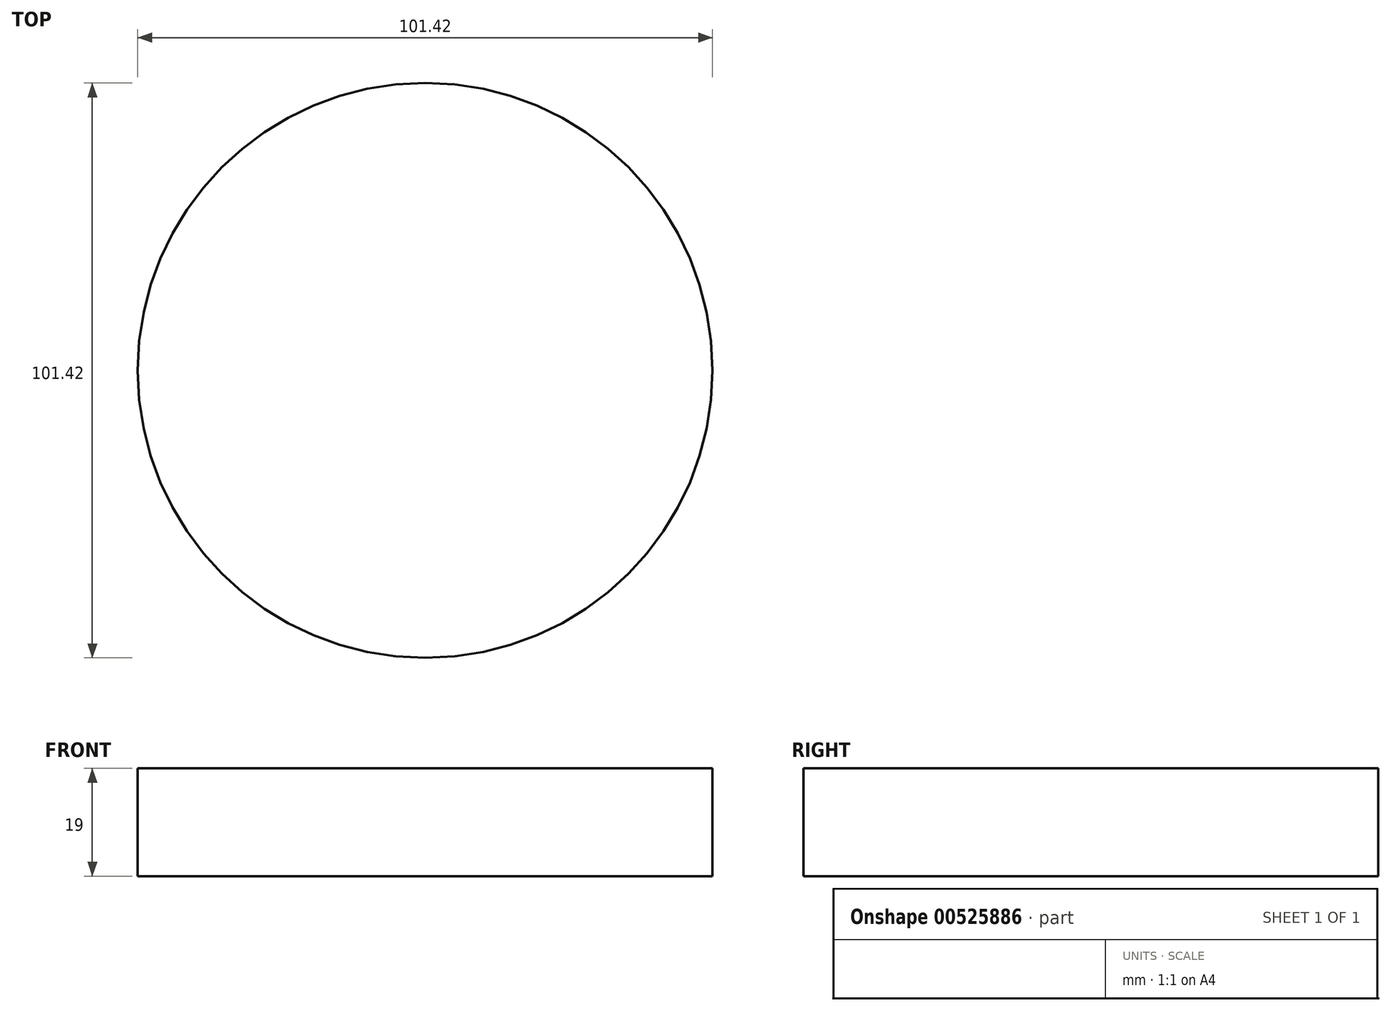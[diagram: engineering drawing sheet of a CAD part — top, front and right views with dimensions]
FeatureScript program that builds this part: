
annotation { "Feature Type Name" : "Feature", "Feature Type Description" : "" }
export const myFeature = defineFeature(function(context is Context, id is Id, definition is map)
    precondition{}
    {
        {
            var Q0;
            Q0=qCreatedBy(makeId("Top.planeOp"),FACE);
            var sketch = newSketch(context, id + "F0", { "sketchPlane" : qUnion([Q0])});
            skCircle(sketch, "E0", {"center": v(0, 0) * mm, "radius": 50.7 * mm});
            skSolve(sketch);
        }
        {
            var Q0;
            Q0 = qSketchRegion(id + "F0", true);
            extrude(context, id + "F1", {"entities" : qUnion([Q0]), "depth" : 19 * mm, "offsetDistance" : 25 * mm});
        }
    });
